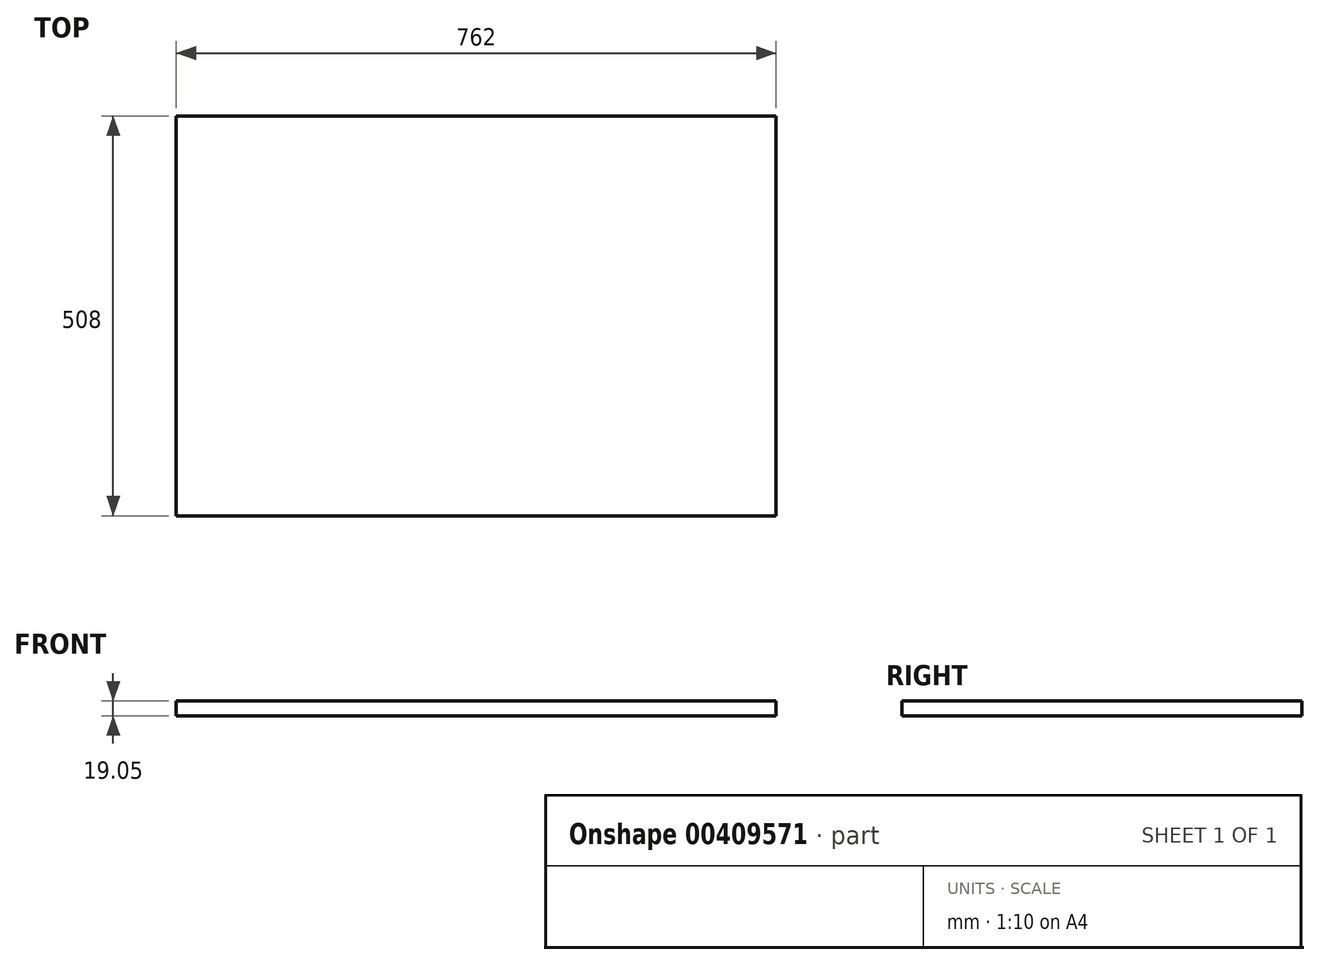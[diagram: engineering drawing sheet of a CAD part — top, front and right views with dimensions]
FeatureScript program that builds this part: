
annotation { "Feature Type Name" : "Feature", "Feature Type Description" : "" }
export const myFeature = defineFeature(function(context is Context, id is Id, definition is map)
    precondition{}
    {
        {
            var Q0;
            Q0=qCreatedBy(makeId("Top.planeOp"),FACE);
            var sketch = newSketch(context, id + "F0", { "sketchPlane" : qUnion([Q0])});
            skLineSegment(sketch, "E0.bottom", {"start": v(-454.84, 331.05) * mm, "end": v(307.16, 331.05) * mm});
            skLineSegment(sketch, "E0.top", {"start": v(-454.84, -176.95) * mm, "end": v(307.16, -176.95) * mm});
            skLineSegment(sketch, "E0.left", {"start": v(-454.84, 331.05) * mm, "end": v(-454.84, -176.95) * mm});
            skLineSegment(sketch, "E0.right", {"start": v(307.16, 331.05) * mm, "end": v(307.16, -176.95) * mm});
            skSolve(sketch);
        }
        {
            var Q0;
            Q0=makeQuery(id+"F0.imprint","IMPRINT",FACE,{"disambiguationData":[TD([[makeQuery(id+"F0.imprint","IMPRINT",EDGE,{"derivedFrom":sQuery(id+"F0.wireOp",EDGE,"E0.bottom")}),-1.0]])]});
            extrude(context, id + "F1", {"entities" : qUnion([Q0]), "depth" : 19.05 * mm});
        }
    });
